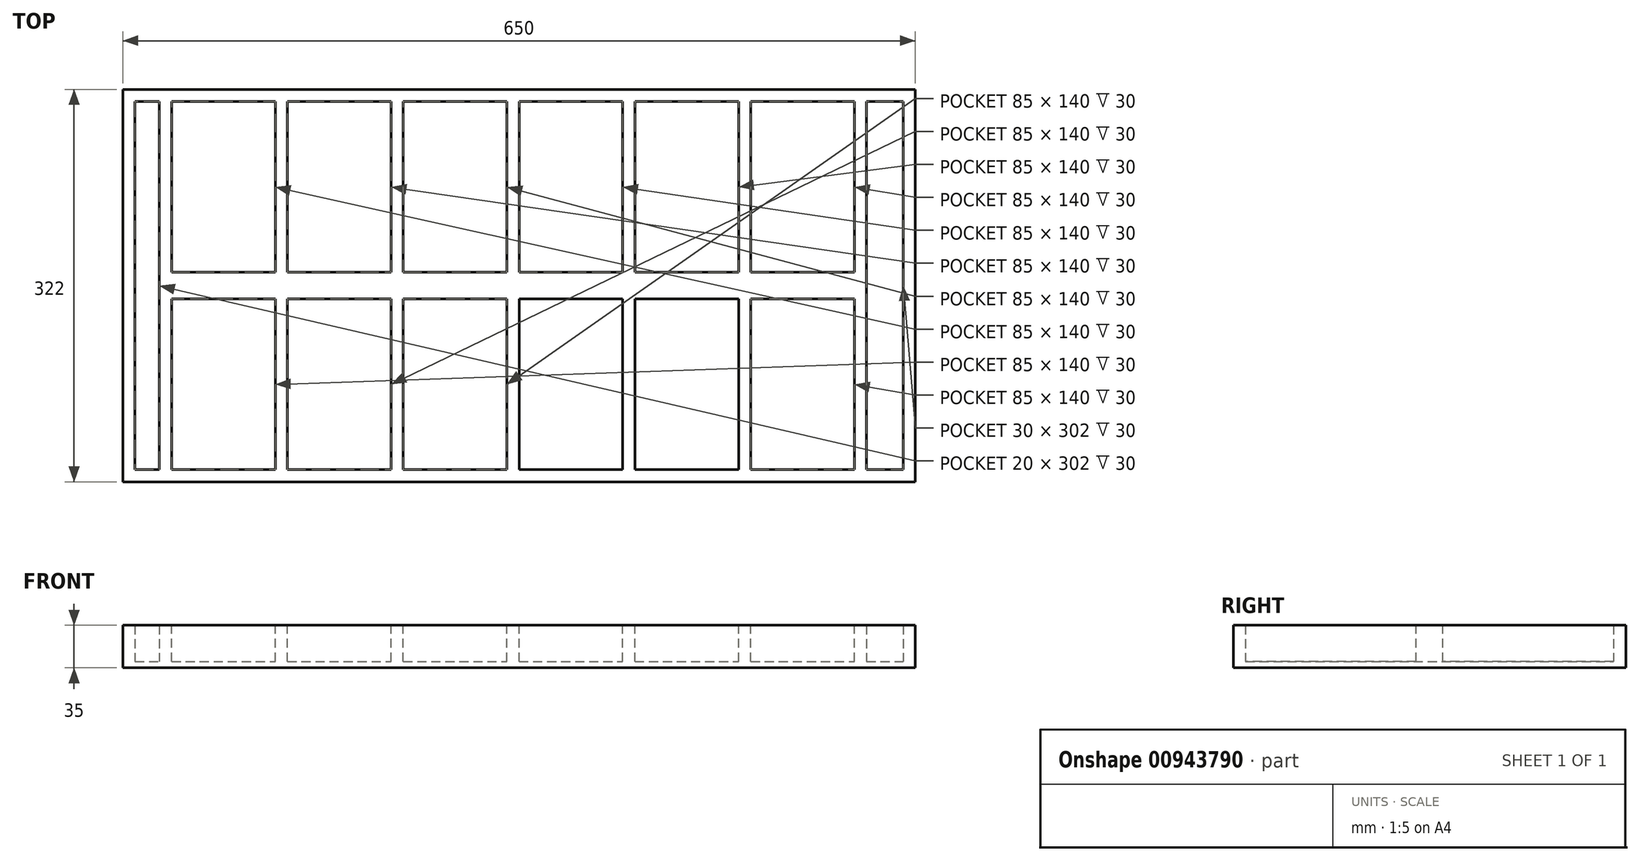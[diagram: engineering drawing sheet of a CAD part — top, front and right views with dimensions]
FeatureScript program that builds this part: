
annotation { "Feature Type Name" : "Feature", "Feature Type Description" : "" }
export const myFeature = defineFeature(function(context is Context, id is Id, definition is map)
    precondition{}
    {
        {
            var Q0;
            Q0=qCreatedBy(makeId("Top.planeOp"),FACE);
            var sketch = newSketch(context, id + "F0", { "sketchPlane" : qUnion([Q0])});
            skLineSegment(sketch, "E0.bottom", {"start": v(-290, 161) * mm, "end": v(290, 161) * mm});
            skLineSegment(sketch, "E0.top", {"start": v(-290, -161) * mm, "end": v(290, -161) * mm});
            skLineSegment(sketch, "E0.left", {"start": v(-290, 161) * mm, "end": v(-290, -161) * mm});
            skLineSegment(sketch, "E0.right", {"start": v(290, 161) * mm, "end": v(290, -161) * mm});
            skPoint(sketch, "E0.middle", {"position": v(0, 0) * mm});
            skSolve(sketch);
        }
        {
            var Q0;
            Q0=qSketchRegion(id+"F0",true);
            extrude(context, id + "F1", {"entities" : qUnion([Q0]), "depth" : 35 * mm, "offsetDistance" : 25 * mm, "symmetric" : true});
        }
        {
            var Q0;
            Q0=qCreatedBy(makeId("Top.planeOp"),FACE);
            var sketch = newSketch(context, id + "F2", { "sketchPlane" : qUnion([Q0])});
            skLineSegment(sketch, "E1.bottom", {"start": v(195, -11) * mm, "end": v(280, -11) * mm});
            skLineSegment(sketch, "E1.top", {"start": v(195, -151) * mm, "end": v(280, -151) * mm});
            skLineSegment(sketch, "E1.left", {"start": v(195, -11) * mm, "end": v(195, -151) * mm});
            skLineSegment(sketch, "E1.right", {"start": v(280, -11) * mm, "end": v(280, -151) * mm});
            skLineSegment(sketch, "E2.1.0.0", {"start": v(100, -11) * mm, "end": v(185, -11) * mm});
            skLineSegment(sketch, "E2.1.0.1", {"start": v(100, -11) * mm, "end": v(100, -151) * mm});
            skLineSegment(sketch, "E2.1.0.2", {"start": v(185, -11) * mm, "end": v(185, -151) * mm});
            skLineSegment(sketch, "E2.1.0.3", {"start": v(100, -151) * mm, "end": v(185, -151) * mm});
            skLineSegment(sketch, "E2.2.0.0", {"start": v(5, -11) * mm, "end": v(90, -11) * mm});
            skLineSegment(sketch, "E2.2.0.1", {"start": v(5, -11) * mm, "end": v(5, -151) * mm});
            skLineSegment(sketch, "E2.2.0.2", {"start": v(90, -11) * mm, "end": v(90, -151) * mm});
            skLineSegment(sketch, "E2.2.0.3", {"start": v(5, -151) * mm, "end": v(90, -151) * mm});
            skLineSegment(sketch, "E2.3.0.0", {"start": v(-90, -11) * mm, "end": v(-5, -11) * mm});
            skLineSegment(sketch, "E2.3.0.1", {"start": v(-90, -11) * mm, "end": v(-90, -151) * mm});
            skLineSegment(sketch, "E2.3.0.2", {"start": v(-5, -11) * mm, "end": v(-5, -151) * mm});
            skLineSegment(sketch, "E2.3.0.3", {"start": v(-90, -151) * mm, "end": v(-5, -151) * mm});
            skLineSegment(sketch, "E2.4.0.0", {"start": v(-185, -11) * mm, "end": v(-100, -11) * mm});
            skLineSegment(sketch, "E2.4.0.1", {"start": v(-185, -11) * mm, "end": v(-185, -151) * mm});
            skLineSegment(sketch, "E2.4.0.2", {"start": v(-100, -11) * mm, "end": v(-100, -151) * mm});
            skLineSegment(sketch, "E2.4.0.3", {"start": v(-185, -151) * mm, "end": v(-100, -151) * mm});
            skLineSegment(sketch, "E2.direction1", {"start": v(195, -151) * mm, "end": v(100, -151) * mm, "construction": true});
            skLineSegment(sketch, "E3", {"start": v(-290, 0) * mm, "end": v(290, 0) * mm, "construction": true});
            skLineSegment(sketch, "E4.MirrorCS", {"start": v(100, 151) * mm, "end": v(185, 151) * mm});
            skLineSegment(sketch, "E5.MirrorCS", {"start": v(280, 11) * mm, "end": v(280, 151) * mm});
            skLineSegment(sketch, "E6.MirrorCS", {"start": v(5, 11) * mm, "end": v(5, 151) * mm});
            skLineSegment(sketch, "E7.MirrorCS", {"start": v(-185, 11) * mm, "end": v(-100, 11) * mm});
            skLineSegment(sketch, "E8.MirrorCS", {"start": v(-185, 11) * mm, "end": v(-185, 151) * mm});
            skLineSegment(sketch, "E9.MirrorCS", {"start": v(195, 151) * mm, "end": v(280, 151) * mm});
            skLineSegment(sketch, "E10.MirrorCS", {"start": v(-100, 11) * mm, "end": v(-100, 151) * mm});
            skLineSegment(sketch, "E11.MirrorCS", {"start": v(100, 11) * mm, "end": v(185, 11) * mm});
            skLineSegment(sketch, "E12.MirrorCS", {"start": v(185, 11) * mm, "end": v(185, 151) * mm});
            skLineSegment(sketch, "E13.MirrorCS", {"start": v(195, 11) * mm, "end": v(280, 11) * mm});
            skLineSegment(sketch, "E14.MirrorCS", {"start": v(-90, 11) * mm, "end": v(-90, 151) * mm});
            skLineSegment(sketch, "E15.MirrorCS", {"start": v(90, 11) * mm, "end": v(90, 151) * mm});
            skLineSegment(sketch, "E16.MirrorCS", {"start": v(195, 151) * mm, "end": v(100, 151) * mm, "construction": true});
            skLineSegment(sketch, "E17.MirrorCS", {"start": v(100, 11) * mm, "end": v(100, 151) * mm});
            skLineSegment(sketch, "E18.MirrorCS", {"start": v(-90, 11) * mm, "end": v(-5, 11) * mm});
            skLineSegment(sketch, "E19.MirrorCS", {"start": v(-185, 151) * mm, "end": v(-100, 151) * mm});
            skLineSegment(sketch, "E20.MirrorCS", {"start": v(5, 11) * mm, "end": v(90, 11) * mm});
            skLineSegment(sketch, "E21.MirrorCS", {"start": v(-5, 11) * mm, "end": v(-5, 151) * mm});
            skLineSegment(sketch, "E22.MirrorCS", {"start": v(195, 11) * mm, "end": v(195, 151) * mm});
            skLineSegment(sketch, "E23.MirrorCS", {"start": v(-90, 151) * mm, "end": v(-5, 151) * mm});
            skLineSegment(sketch, "E24.MirrorCS", {"start": v(5, 151) * mm, "end": v(90, 151) * mm});
            skLineSegment(sketch, "E25", {"start": v(-280, 161) * mm, "end": v(-280, -161) * mm, "construction": true});
            skLineSegment(sketch, "E26.bottom", {"start": v(-280, 151) * mm, "end": v(-195, 151) * mm});
            skLineSegment(sketch, "E26.top", {"start": v(-280, 11) * mm, "end": v(-195, 11) * mm});
            skLineSegment(sketch, "E26.left", {"start": v(-280, 151) * mm, "end": v(-280, 11) * mm});
            skLineSegment(sketch, "E26.right", {"start": v(-195, 151) * mm, "end": v(-195, 11) * mm});
            skLineSegment(sketch, "E27.bottom", {"start": v(-280, -11) * mm, "end": v(-195, -11) * mm});
            skLineSegment(sketch, "E27.top", {"start": v(-280, -151) * mm, "end": v(-195, -151) * mm});
            skLineSegment(sketch, "E27.left", {"start": v(-280, -11) * mm, "end": v(-280, -151) * mm});
            skLineSegment(sketch, "E27.right", {"start": v(-195, -11) * mm, "end": v(-195, -151) * mm});
            skLineSegment(sketch, "E28", {"start": v(-185, 151) * mm, "end": v(-290, 151) * mm, "construction": true});
            skLineSegment(sketch, "E29", {"start": v(-185, -151) * mm, "end": v(-290, -151) * mm, "construction": true});
            skLineSegment(sketch, "E30", {"start": v(-195, 151) * mm, "end": v(-195, -151) * mm, "construction": true});
            skPoint(sketch, "E31", {"position": v(-280, 151) * mm});
            skPoint(sketch, "E32", {"position": v(-280, -151) * mm});
            skLineSegment(sketch, "E33", {"start": v(-290, 11) * mm, "end": v(-195, 11) * mm, "construction": true});
            skLineSegment(sketch, "E34", {"start": v(-290, -11) * mm, "end": v(-195, -11) * mm, "construction": true});
            skPoint(sketch, "E35", {"position": v(-280, -11) * mm});
            skSolve(sketch);
        }
        {
            var Q0;
            Q0=qSketchRegion(id+"F2",true);
            extrude(context, id + "F3", {"entities" : qUnion([Q0]), "operationType" : NewBodyOperationType.REMOVE, "oppositeDirection" : true, "depth" : 50 * mm, "offsetDistance" : 25 * mm, "symmetric" : true});
        }
        {
            var Q0;
            Q0=makeQuery(id+"F1.opExtrude","SWEPT_FACE",FACE,{"disambiguationData":[OSD([sQuery(id+"F0.wireOp",EDGE,"E0.left")])]});
            var sketch = newSketch(context, id + "F4", { "sketchPlane" : qUnion([Q0])});
            skLineSegment(sketch, "E36.bottom", {"start": v(-161, -17.5) * mm, "end": v(161, -17.5) * mm});
            skLineSegment(sketch, "E36.top", {"start": v(-161, 17.5) * mm, "end": v(161, 17.5) * mm});
            skLineSegment(sketch, "E36.left", {"start": v(-161, -17.5) * mm, "end": v(-161, 17.5) * mm});
            skLineSegment(sketch, "E36.right", {"start": v(161, -17.5) * mm, "end": v(161, 17.5) * mm});
            skPoint(sketch, "E36.middle", {"position": v(0, 0) * mm});
            skSolve(sketch);
        }
        {
            var Q0;
            Q0=qSketchRegion(id+"F4",true);
            extrude(context, id + "F5", {"entities" : qUnion([Q0]), "depth" : 30 * mm, "offsetDistance" : 25 * mm});
        }
        {
            var Q0;
            Q0=makeQuery(id+"F5.opExtrude","SWEPT_FACE",FACE,{"disambiguationData":[OSD([sQuery(id+"F4.wireOp",EDGE,"E36.bottom")])]});
            var sketch = newSketch(context, id + "F6", { "sketchPlane" : qUnion([Q0])});
            skLineSegment(sketch, "E37.bottom", {"start": v(-290, -151) * mm, "end": v(-310, -151) * mm});
            skLineSegment(sketch, "E37.top", {"start": v(-290, 151) * mm, "end": v(-310, 151) * mm});
            skLineSegment(sketch, "E37.left", {"start": v(-290, -151) * mm, "end": v(-290, 151) * mm});
            skLineSegment(sketch, "E37.right", {"start": v(-310, -151) * mm, "end": v(-310, 151) * mm});
            skSolve(sketch);
        }
        {
            var Q0;
            Q0=qSketchRegion(id+"F6",true);
            extrude(context, id + "F7", {"entities" : qUnion([Q0]), "operationType" : NewBodyOperationType.REMOVE, "endBound" : BoundingType.THROUGH_ALL, "oppositeDirection" : true, "depth" : 25 * mm, "offsetDistance" : 25 * mm});
        }
        {
            var Q0;
            Q0=makeQuery(id+"F1.opExtrude","SWEPT_FACE",FACE,{"disambiguationData":[OSD([sQuery(id+"F0.wireOp",EDGE,"E0.right")])]});
            var sketch = newSketch(context, id + "F8", { "sketchPlane" : qUnion([Q0])});
            skLineSegment(sketch, "E38.bottom", {"start": v(-161, 17.5) * mm, "end": v(161, 17.5) * mm});
            skLineSegment(sketch, "E38.top", {"start": v(-161, -17.5) * mm, "end": v(161, -17.5) * mm});
            skLineSegment(sketch, "E38.left", {"start": v(-161, 17.5) * mm, "end": v(-161, -17.5) * mm});
            skLineSegment(sketch, "E38.right", {"start": v(161, 17.5) * mm, "end": v(161, -17.5) * mm});
            skPoint(sketch, "E38.middle", {"position": v(0, 0) * mm});
            skSolve(sketch);
        }
        {
            var Q0;
            Q0=qSketchRegion(id+"F8",true);
            extrude(context, id + "F9", {"entities" : qUnion([Q0]), "depth" : 40 * mm, "offsetDistance" : 25 * mm});
        }
        {
            var Q0;
            Q0=makeQuery(id+"F9.opExtrude","SWEPT_FACE",FACE,{"disambiguationData":[OSD([sQuery(id+"F8.wireOp",EDGE,"E38.top")])]});
            var sketch = newSketch(context, id + "F10", { "sketchPlane" : qUnion([Q0])});
            skLineSegment(sketch, "E39", {"start": v(290, 151) * mm, "end": v(320, 151) * mm});
            skLineSegment(sketch, "E40", {"start": v(320, 151) * mm, "end": v(320, -151) * mm});
            skLineSegment(sketch, "E41", {"start": v(320, -151) * mm, "end": v(290, -151) * mm});
            skSolve(sketch);
        }
        {
            var Q0;
            Q0=qSketchRegion(id+"F10",true);
            var Q1;
            {var subQ0=sQuery(id+"F10.wireOp",EDGE,"E39");Q1=makeQuery(id+"F10.imprint","IMPRINT",FACE,{"disambiguationData":[TD([[makeQuery(id+"F10.imprint","IMPRINT",EDGE,{"derivedFrom":subQ0}),-1.0]])]});}
            extrude(context, id + "F11", {"entities" : qUnion([Q0, Q1]), "operationType" : NewBodyOperationType.REMOVE, "endBound" : BoundingType.THROUGH_ALL, "oppositeDirection" : true, "depth" : 25 * mm, "offsetDistance" : 25 * mm});
        }
        {
            var Q0;
            Q0=makeQuery(id+"F5.opExtrude","SWEPT_BODY",BODY,{"disambiguationData":[OSD([sQuery(id+"F4.wireOp",EDGE,"E36.bottom"),sQuery(id+"F4.wireOp",EDGE,"E36.top"),sQuery(id+"F4.wireOp",EDGE,"E36.left"),sQuery(id+"F4.wireOp",EDGE,"E36.right")])]});
            var Q1;
            Q1=makeQuery(id+"F1.opExtrude","SWEPT_BODY",BODY,{"disambiguationData":[OSD([sQuery(id+"F0.wireOp",EDGE,"E0.bottom"),sQuery(id+"F0.wireOp",EDGE,"E0.top"),sQuery(id+"F0.wireOp",EDGE,"E0.left"),sQuery(id+"F0.wireOp",EDGE,"E0.right")])]});
            var Q2;
            Q2=makeQuery(id+"F9.opExtrude","SWEPT_BODY",BODY,{"disambiguationData":[OSD([sQuery(id+"F8.wireOp",EDGE,"E38.bottom"),sQuery(id+"F8.wireOp",EDGE,"E38.top"),sQuery(id+"F8.wireOp",EDGE,"E38.left"),sQuery(id+"F8.wireOp",EDGE,"E38.right")])]});
            booleanBodies(context, id + "F12", {"operationType" : BooleanOperationType.UNION, "tools" : qUnion([Q0, Q1, Q2])});
        }
        {
            var Q0;
            Q0=makeQuery(id+"F12.opBoolean","MERGE",FACE,{"derivedFrom":[makeQuery(id+"F1.opExtrude","CAP_FACE",FACE,{"disambiguationData":[OSD([sQuery(id+"F0.wireOp",EDGE,"E0.bottom"),sQuery(id+"F0.wireOp",EDGE,"E0.top"),sQuery(id+"F0.wireOp",EDGE,"E0.left"),sQuery(id+"F0.wireOp",EDGE,"E0.right")])],"isStart":true}),makeQuery(id+"F5.opExtrude","SWEPT_FACE",FACE,{"disambiguationData":[OSD([sQuery(id+"F4.wireOp",EDGE,"E36.bottom")])]}),makeQuery(id+"F9.opExtrude","SWEPT_FACE",FACE,{"disambiguationData":[OSD([sQuery(id+"F8.wireOp",EDGE,"E38.top")])]})]});
            var sketch = newSketch(context, id + "F13", { "sketchPlane" : qUnion([Q0])});
            skLineSegment(sketch, "E42", {"start": v(320, 0) * mm, "end": v(-320, 0) * mm, "construction": true});
            skLineSegment(sketch, "E43", {"start": v(185, -75.62) * mm, "end": v(185, 62.33) * mm, "construction": true});
            skLineSegment(sketch, "E44", {"start": v(100, -75.62) * mm, "end": v(100, 63.74) * mm, "construction": true});
            skPoint(sketch, "E45", {"position": v(185, 0) * mm});
            skPoint(sketch, "E46", {"position": v(100, 0) * mm});
            skPoint(sketch, "E47", {"position": v(142.5, 0) * mm});
            skLineSegment(sketch, "E48", {"start": v(-90, -11) * mm, "end": v(-100, 11) * mm, "construction": true});
            skLineSegment(sketch, "E49", {"start": v(-100, -11) * mm, "end": v(-90, 11) * mm, "construction": true});
            skPoint(sketch, "E50", {"position": v(-95, 0) * mm});
            skLineSegment(sketch, "E51", {"start": v(-195, -11) * mm, "end": v(-185, 11) * mm, "construction": true});
            skPoint(sketch, "E52", {"position": v(-190, 0) * mm});
            skLineSegment(sketch, "E53", {"start": v(90, -32.12) * mm, "end": v(90, 28.55) * mm, "construction": true});
            skLineSegment(sketch, "E54", {"start": v(5, -26.43) * mm, "end": v(5, 35.5) * mm, "construction": true});
            skLineSegment(sketch, "E55", {"start": v(50, -39.7) * mm, "end": v(50, 30.45) * mm, "construction": true});
            skPoint(sketch, "E56", {"position": v(50, 0) * mm});
            skLineSegment(sketch, "E57.bottom", {"start": v(320, -151) * mm, "end": v(-310, -151) * mm});
            skLineSegment(sketch, "E57.top", {"start": v(320, 151) * mm, "end": v(-310, 151) * mm});
            skLineSegment(sketch, "E57.left", {"start": v(320, -151) * mm, "end": v(320, 151) * mm});
            skLineSegment(sketch, "E57.right", {"start": v(-310, -151) * mm, "end": v(-310, 151) * mm});
            skSolve(sketch);
        }
        {
            var Q0;
            Q0 = qSketchRegion(id + "F13", true);
            extrude(context, id + "F14", {"entities" : qUnion([Q0]), "operationType" : NewBodyOperationType.ADD, "oppositeDirection" : true, "depth" : 5 * mm, "offsetDistance" : 25 * mm});
        }
    });
